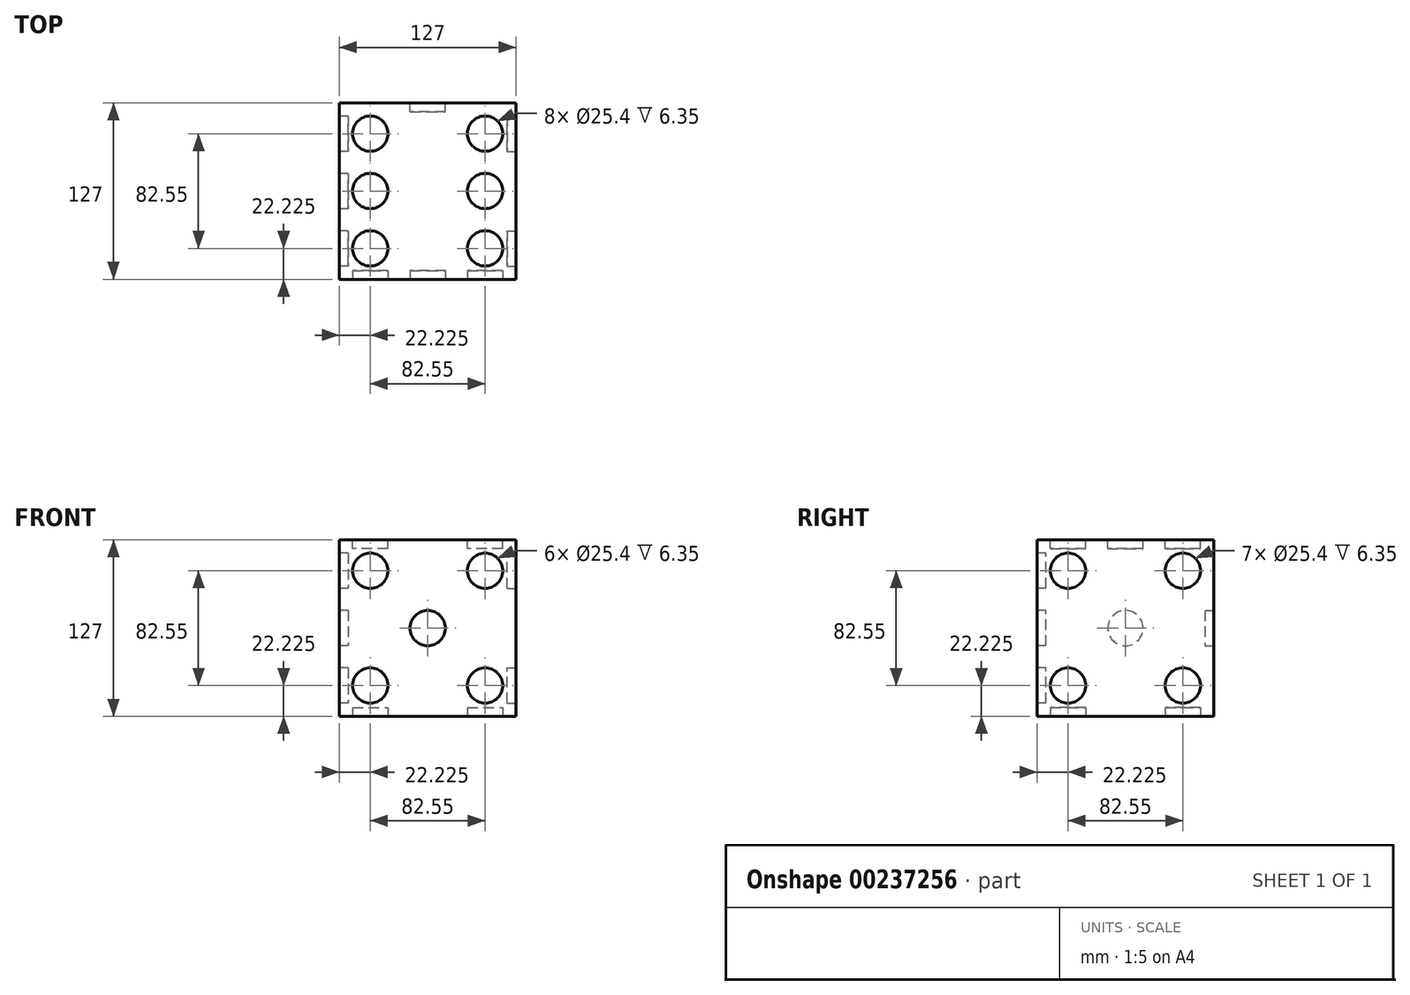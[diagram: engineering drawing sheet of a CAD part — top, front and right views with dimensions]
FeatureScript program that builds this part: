
annotation { "Feature Type Name" : "Feature", "Feature Type Description" : "" }
export const myFeature = defineFeature(function(context is Context, id is Id, definition is map)
    precondition{}
    {
        {
            var Q0;
            Q0=qCreatedBy(makeId("Top.planeOp"),FACE);
            var sketch = newSketch(context, id + "F0", { "sketchPlane" : qUnion([Q0])});
            skLineSegment(sketch, "E0.bottom", {"start": v(0, 0) * mm, "end": v(127, 0) * mm});
            skLineSegment(sketch, "E0.top", {"start": v(0, 127) * mm, "end": v(127, 127) * mm});
            skLineSegment(sketch, "E0.left", {"start": v(0, 0) * mm, "end": v(0, 127) * mm});
            skLineSegment(sketch, "E0.right", {"start": v(127, 0) * mm, "end": v(127, 127) * mm});
            skSolve(sketch);
        }
        {
            var Q0;
            Q0 = qSketchRegion(id + "F0", true);
            extrude(context, id + "F1", {"entities" : qUnion([Q0]), "depth" : 127 * mm});
        }
        {
            var Q0;
            Q0=makeQuery(id+"F1.opExtrude","SWEPT_FACE",FACE,{"disambiguationData":[OSD([sQuery(id+"F0.wireOp",EDGE,"E0.top")])]});
            var sketch = newSketch(context, id + "F2", { "sketchPlane" : qUnion([Q0])});
            skCircle(sketch, "E1", {"center": v(-63.5, 63.5) * mm, "radius": 12.7 * mm});
            skSolve(sketch);
        }
        {
            var Q0;
            Q0 = qSketchRegion(id + "F2", true);
            extrude(context, id + "F3", {"entities" : qUnion([Q0]), "operationType" : NewBodyOperationType.REMOVE, "oppositeDirection" : true, "depth" : 6.35 * mm});
        }
        {
            var Q0;
            Q0=makeQuery(id+"F1.opExtrude","CAP_FACE",FACE,{"disambiguationData":[OSD([sQuery(id+"F0.wireOp",EDGE,"E0.bottom"),sQuery(id+"F0.wireOp",EDGE,"E0.top"),sQuery(id+"F0.wireOp",EDGE,"E0.left"),sQuery(id+"F0.wireOp",EDGE,"E0.right")])],"isStart":true});
            var sketch = newSketch(context, id + "F4", { "sketchPlane" : qUnion([Q0])});
            skCircle(sketch, "E2", {"center": v(104.78, -22.23) * mm, "radius": 12.7 * mm});
            skCircle(sketch, "E3", {"center": v(22.23, -104.78) * mm, "radius": 12.7 * mm});
            skSolve(sketch);
        }
        {
            var Q0;
            Q0 = qSketchRegion(id + "F4", true);
            extrude(context, id + "F5", {"entities" : qUnion([Q0]), "operationType" : NewBodyOperationType.REMOVE, "oppositeDirection" : true, "depth" : 6.35 * mm});
        }
        {
            var Q0;
            Q0=makeQuery(id+"F1.opExtrude","SWEPT_FACE",FACE,{"disambiguationData":[OSD([sQuery(id+"F0.wireOp",EDGE,"E0.left")])]});
            var sketch = newSketch(context, id + "F6", { "sketchPlane" : qUnion([Q0])});
            skLineSegment(sketch, "E4", {"start": v(0, 0) * mm, "end": v(-127, 127) * mm, "construction": true});
            skLineSegment(sketch, "E5", {"start": v(-127, 127) * mm, "end": v(-69.12, 69.12) * mm, "construction": true});
            skCircle(sketch, "E6", {"center": v(-22.23, 22.22) * mm, "radius": 12.7 * mm});
            skCircle(sketch, "E7", {"center": v(-63.5, 63.5) * mm, "radius": 12.7 * mm});
            skCircle(sketch, "E8", {"center": v(-104.78, 104.78) * mm, "radius": 12.7 * mm});
            skSolve(sketch);
        }
        {
            var Q0;
            Q0 = qSketchRegion(id + "F6", true);
            extrude(context, id + "F7", {"entities" : qUnion([Q0]), "operationType" : NewBodyOperationType.REMOVE, "oppositeDirection" : true, "depth" : 6.35 * mm});
        }
        {
            var Q0;
            Q0=makeQuery(id+"F1.opExtrude","SWEPT_FACE",FACE,{"disambiguationData":[OSD([sQuery(id+"F0.wireOp",EDGE,"E0.right")])]});
            var sketch = newSketch(context, id + "F8", { "sketchPlane" : qUnion([Q0])});
            skCircle(sketch, "E9", {"center": v(22.23, 22.22) * mm, "radius": 12.7 * mm});
            skCircle(sketch, "E10", {"center": v(104.78, 22.22) * mm, "radius": 12.7 * mm});
            skCircle(sketch, "E11", {"center": v(22.23, 104.78) * mm, "radius": 12.7 * mm});
            skCircle(sketch, "E12", {"center": v(104.78, 104.78) * mm, "radius": 12.7 * mm});
            skSolve(sketch);
        }
        {
            var Q0;
            Q0 = qSketchRegion(id + "F8", true);
            extrude(context, id + "F9", {"entities" : qUnion([Q0]), "operationType" : NewBodyOperationType.REMOVE, "oppositeDirection" : true, "depth" : 6.35 * mm});
        }
        {
            var Q0;
            Q0=makeQuery(id+"F1.opExtrude","SWEPT_FACE",FACE,{"disambiguationData":[OSD([sQuery(id+"F0.wireOp",EDGE,"E0.bottom")])]});
            var sketch = newSketch(context, id + "F10", { "sketchPlane" : qUnion([Q0])});
            skCircle(sketch, "E13", {"center": v(63.5, 63.5) * mm, "radius": 12.7 * mm});
            skCircle(sketch, "E14", {"center": v(22.23, 104.78) * mm, "radius": 12.7 * mm});
            skCircle(sketch, "E15", {"center": v(22.23, 22.22) * mm, "radius": 12.7 * mm});
            skCircle(sketch, "E16", {"center": v(104.78, 104.78) * mm, "radius": 12.7 * mm});
            skCircle(sketch, "E17", {"center": v(104.78, 22.22) * mm, "radius": 12.7 * mm});
            skSolve(sketch);
        }
        {
            var Q0;
            Q0 = qSketchRegion(id + "F10", true);
            extrude(context, id + "F11", {"entities" : qUnion([Q0]), "operationType" : NewBodyOperationType.REMOVE, "oppositeDirection" : true, "depth" : 6.35 * mm});
        }
        {
            var Q0;
            Q0=makeQuery(id+"F1.opExtrude","CAP_FACE",FACE,{"disambiguationData":[OSD([sQuery(id+"F0.wireOp",EDGE,"E0.bottom"),sQuery(id+"F0.wireOp",EDGE,"E0.top"),sQuery(id+"F0.wireOp",EDGE,"E0.left"),sQuery(id+"F0.wireOp",EDGE,"E0.right")])],"isStart":false});
            var sketch = newSketch(context, id + "F12", { "sketchPlane" : qUnion([Q0])});
            skCircle(sketch, "E18", {"center": v(104.78, 63.5) * mm, "radius": 12.7 * mm});
            skCircle(sketch, "E19", {"center": v(104.78, 22.23) * mm, "radius": 12.7 * mm});
            skCircle(sketch, "E20", {"center": v(104.78, 104.78) * mm, "radius": 12.7 * mm});
            skCircle(sketch, "E21", {"center": v(22.23, 22.23) * mm, "radius": 12.7 * mm});
            skCircle(sketch, "E22", {"center": v(22.23, 63.5) * mm, "radius": 12.7 * mm});
            skCircle(sketch, "E23", {"center": v(22.23, 104.78) * mm, "radius": 12.7 * mm});
            skSolve(sketch);
        }
        {
            var Q0;
            Q0 = qSketchRegion(id + "F12", true);
            extrude(context, id + "F13", {"entities" : qUnion([Q0]), "operationType" : NewBodyOperationType.REMOVE, "oppositeDirection" : true, "depth" : 6.35 * mm});
        }
    });
